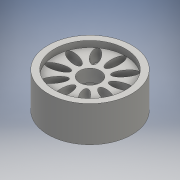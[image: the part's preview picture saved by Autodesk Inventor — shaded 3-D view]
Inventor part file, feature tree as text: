
AUTODESK INVENTOR PART (.ipt)
format: ipt  version: 2016 (Build 200138000, 138)  size: 196,096 bytes
history: native  units: mm
features: extrude x4, sketch x2, projected_geometry x2, other x1
ambient origin geometry x8: Origin, YZ Plane, XZ Plane, XY Plane, X Axis, Y Axis, Z Axis, Center Point
bodies: Body1 (feature_tree)
feature tree (9):
  other  "ソリッド1"
  sketch  "スケッチ1"
  extrude  "押し出し1"  Depth=20.0mm
  extrude  "押し出し2"  Depth=11.6mm
  sketch  "スケッチ2"
  extrude  "押し出し3"  Depth=8.5mm TaperAngle=0.0deg
  extrude  "押し出し4"  Depth=4.0mm TaperAngle=0.0deg
  projected_geometry  "投影ループ1"
  projected_geometry  "投影ループ2"
